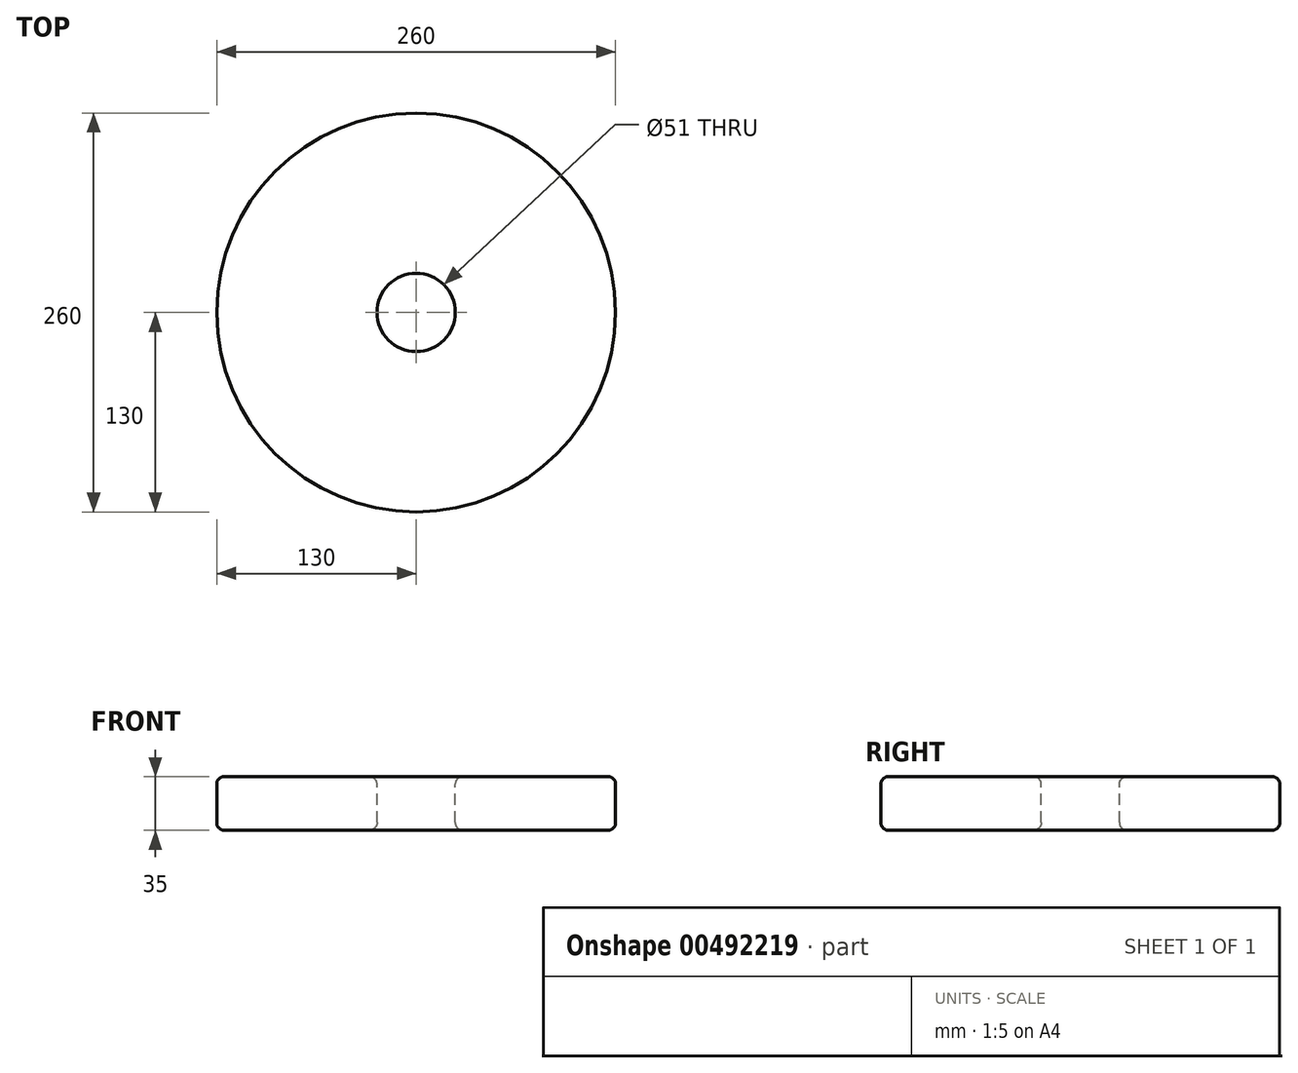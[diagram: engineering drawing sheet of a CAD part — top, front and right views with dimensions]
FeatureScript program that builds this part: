
annotation { "Feature Type Name" : "Feature", "Feature Type Description" : "" }
export const myFeature = defineFeature(function(context is Context, id is Id, definition is map)
    precondition{}
    {
        {
            var Q0;
            Q0=qCreatedBy(makeId("Top.planeOp"),FACE);
            var sketch = newSketch(context, id + "F0", { "sketchPlane" : qUnion([Q0])});
            skCircle(sketch, "E0", {"center": v(0, 0) * mm, "radius": 25.5 * mm});
            skCircle(sketch, "E1", {"center": v(0, 0) * mm, "radius": 130 * mm});
            skSolve(sketch);
        }
        {
            var Q0;
            Q0 = qSketchRegion(id + "F0", true);
            extrude(context, id + "F1", {"entities" : qUnion([Q0]), "oppositeDirection" : true, "depth" : 35 * mm});
        }
        {
            var Q0;
            Q0=makeQuery(id+"F1.opExtrude","CAP_EDGE",EDGE,{"disambiguationData":[OSD([sQuery(id+"F0.wireOp",EDGE,"E1")])],"isStart":true});
            var Q1;
            Q1=makeQuery(id+"F1.opExtrude","CAP_EDGE",EDGE,{"disambiguationData":[OSD([sQuery(id+"F0.wireOp",EDGE,"E1")])],"isStart":false});
            var Q2;
            Q2=makeQuery(id+"F1.opExtrude","CAP_EDGE",EDGE,{"disambiguationData":[OSD([sQuery(id+"F0.wireOp",EDGE,"E0")])],"isStart":true});
            var Q3;
            Q3=makeQuery(id+"F1.opExtrude","CAP_EDGE",EDGE,{"disambiguationData":[OSD([sQuery(id+"F0.wireOp",EDGE,"E0")])],"isStart":false});
            fillet(context, id + "F2", {"entities" : qUnion([Q0, Q1, Q2, Q3]), "radius" : 5 * mm, "tangentPropagation" : true, "allowEdgeOverflow" : false});
        }
    });
